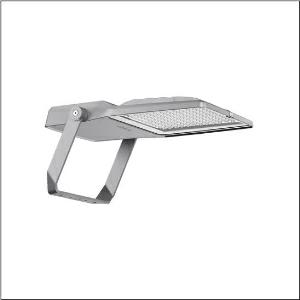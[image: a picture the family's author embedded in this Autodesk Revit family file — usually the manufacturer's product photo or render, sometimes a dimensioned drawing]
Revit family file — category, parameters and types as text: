
# Revit family: floodlight_fl_21_iq_midi___rs12_5xa7781f6b1a_422c
name_source: partatom
category: Lighting Fixtures
units: mm (PartAtom-declared; Revit-internal decimal feet)

## family parameters
Cut with Voids When Loaded = No
Host = Face
Light Source = No
Part Type = Normal
Room Calculation Point = No
Round Connector Dimension = Use Diameter
Shared = No

## types (1)
- --- (1 x LED, 28520 lm, 270.2 W, 5700K)
    Apparent Load = 270 VA
    CIE Flux Codes = 79 92 99 100 100
    Color Rendering = 90
    Color Temperature = 5700K
    Default Elevation = 1800 mm
    Description = Floodlight FL 21 iQ midi, floodlight, primary light control with lens, of PMMA, primary optical cover: protective disc, of toughened safety glass, transparent, light distribution: RS12, light emission: direct distribution, installation type: surface-mounted, LED, High Power LED, rated luminous flux: 28.520lm, luminous efficacy: 106lm/W, light colour: 957, colour temperature: 5700K, control gear: ECG iQ, control: optimised constant luminous flux control (CLO 2.0), Desk-Remote (wireless, voltage-free reading and setting of iQ features in the workshop via application-optimized NFC function/RFID function), Light-Fading, Smart-Wire, Night-Set, Lumen-Switch, Temp-Guard, Auto-Match, with terminal, 6-pole, mains connection: 220..240V, AC, 50/60Hz, start of lifetime: 270W, end of service life: 287W, reduction: 117W, luminaire housing, of diecast aluminium, powder-coated, Siteco® metallic grey (DB 702S), corrosivity category C5 mid according to DIN EN ISO 12944, sealing non-destructively replaceable, mounting bracket, of steel, galvanised, powder-coated, Siteco® metallic grey (DB 702S), protection rating (complete): IP66, insulation class (complete): insulation class II (safety insulation), certification: CE, protection symbol: D, impact resistance: IK08, permissible operating ambient temperature: -40..+40°C, permissible operating ambient temperature for outdoor applications: -40..+50°C, standard: DIN EN 12944, LABS conformity tested according to VDMA 24364:2018-05, packaging unit: 1 piece

Light Distribution: RS12
    Height = 76 mm
    Lamp = 1 x LED
    Lamp Light Flux = 28520 lm
    Lamp Power = 270.2 W
    Lamp count = 1
    Length = 657 mm
    Luminous efficacy = 106 lm/W
    Manufacturer = Siteco
    ModVariant = No
    Model = 5XA7781F6B1A
    Number of Poles = 1
    OnlyDefault = Yes
    Power Factor = 1
    Product Name = Floodlight FL 21 iQ midi | RS12
    Product group = floodlight | pylon annexe
    ProductGroupID = 6200
    Protection Class = Protection class II
    Protection Degree = IP 66
    RLX_Detail_Level = 1
    RLX_Emergency_Light_Flux = 0 lm
    RLX_Emergency_Type = 0
    RLX_Emergency_Type_DB = No
    RlxData = <blob elided: 140961 chars, md5=2bfb9d2d>
    Socket = socket
    Standby Power = 0 W
    System Light Flux = 28520 lm
    System Power = 270 W
    Type Comments = factory setting: luminous flux: 100 % | dim-lin: 254 | 620 mA
    Type Image = l_1006876.jpg
    URL = http://relux.com
    VarID = @adj_037489
    Voltage = 0 V
    Weight = 0.00 kg
    Width = 442 mm

## geometry (parser evidence)
native form markers: Blend x4, Sweep x12
no freeform markers — native parametric forms only
